# Revit family: Furniture_Tables_Svedholm_Curve-Circle-Round
name_source: partatom
category: Furniture
revit_build: Autodesk Revit 2018 (Build: 20190510_1515(x64)
units: mm (PartAtom-declared; Revit-internal decimal feet)

## family parameters
Always vertical = No
Cut with Voids When Loaded = No
OmniClass Number = 23.21.23.00
OmniClass Title = Residential Furniture and Equipment
Room Calculation Point = No
Shared = No
Work Plane-Based = Yes

## types (2) — shared parameters
BIMobject category = Tables
Default Elevation = 1219 mm
Description = Playful tables made of powder coated aluminium that can be combined in many ways. All colours are available upon request.
Design country = Sweden
Detail material = Svedholm - Metal - RAL 9005 Jet black
Edition number = 1
IFC Classification = Furniture
Manufacturer = Svedholm
Manufacturer country = Sweden
Manufacturer name = Svedholm
Material main = Aluminium
Material secondary = Powder coated steel
OmniClass Code = 23-21 23 00
OmniClass Description = Residential Furniture and Equipment
Product Guid = 3f9c0dc3-2379-47d9-865d-9c67c429aa29
Product SKU = Curve-Circle-Round
Product data url = https://bimobject.com
Product family = Curve
Product group = Table
Product name = Curve Circle/Round
Product url = https://www.svedholm.se
QR code = https://bimobject.com
UNSPSC Code = 56
URL = https://www.svedholm.se
Uniclass 1.4 Code = L8221
Uniclass 1.4 Description = Tables

## per-type parameters (varying)
| type | Model | Rectangular - 020 | Round - 010 |
| ART - (311.600.020) | Curve Square | Yes | No |
| ART - (311.600.010) | Curve Round | No | Yes |

## geometry (parser evidence)
native form markers: Sweep x3
no freeform markers — native parametric forms only
